# Revit family: oventrop_cocon-qtr_1146112-16rfa
name_source: partatom
category: Арматура трубопроводов
revit_build: Autodesk Revit 2017 (Build: 20160225_1515(x64)
units: mm (PartAtom-declared; Revit-internal decimal feet)

## family parameters
Всегда вертикально = Да
Заголовок OmniClass = Adjusting/Controlling Valves for Liquid Services
На основе рабочей плоскости = Нет
Номер OmniClass = 23.65.55.14.17
Общий = Нет
При загрузке вырезать с полостями = Нет
Размер круглого соединителя = Использовать радиус
Тип детали = Клапан - Вставляется

## types (2) — shared parameters
Angle = 50.00°
Article Description = Flow control valve
Article Type = Cocon QTR Female-Female 11461
BonnetPlastic = Color RGB 35-35-35
Bronze = Color RGB 156-122-90
Custom = Нет
D_Bonnet = 104 мм
Dist_elem = 30 мм
EMCS Version = 2.0
ETIM Article Class = EC011435
Family Version = 10.14
Hb2 = 50 мм
Hb3 = 5 мм
Hb4 = 18 мм
Hb5 = 3 мм
Hlp1 = 22 мм
IFCExportAs = IfcValveType
IFCExportType = REGULATING
Lgt2 = 11 мм
MEPcontent Class = VALVE_CONTROL
Manufacturer URL = http://www.oventrop.de
Pressure Drop = 0.0 Па
Product Line = Oventrop
R1_Bonnet = 23.026 мм
R2_Bonnet = 31.2 мм
Rcut_Bonnet = 22.026 мм
Revit Version = 2015
r1 = 2 мм
r2 = 3 мм
r3_Bonnet = 14.857 мм
Группа модели = Cocon QTR Female-Female 11461
Изготовитель = Oventrop
Описание = Flow control valve

## per-type parameters (varying)
| type | Female_Port_Width | GTIN | H1_Bonnet | H_Bonnet | Hb1 | Hb6 | Height | L2 | Length | Lgt1 | Manufacturer Art. No. | NominalDiameter | Nut_Dimension | OuterDiameter | Rad1 | Rad2 | Rad3 | Rad4 | Rad5 | SW2 | URL |
| DN 40 | 19.1 мм | 4026755353051 | 59.29 мм | 245 мм | 311.434 мм | 67.186 мм | 245 мм | 8.883 мм | 120 мм | 21.1 мм | 1146112 | 38.100 мм | 54 мм | 48.3 мм | 19.05 мм | 19.05 мм | 21.55 мм | 24.05 мм | 26.05 мм | 62.354 мм | www.stabiplan.com |
| DN 50 | 25.7 мм | 4026755372458 | 61.71 мм | 255 мм | 324.488 мм | 63.503 мм | 255 мм | 11.844 мм | 150 мм | 27.7 мм | 1146116 | 50.800 мм | 70 мм | 60.3 мм | 25.4 мм | 25.4 мм | 27.9 мм | 30.4 мм | 32.4 мм | 80.829 мм | http://file-system.ru |

## geometry (parser evidence)
native form markers: Sweep x7
no freeform markers — native parametric forms only
